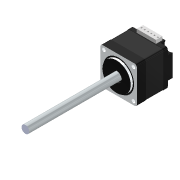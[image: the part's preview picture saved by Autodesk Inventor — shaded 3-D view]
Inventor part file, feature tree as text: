
AUTODESK INVENTOR PART (.ipt)
format: ipt  version: 2022 (Build 260153000, 153)  size: 203,264 bytes
history: mixed  units: mm
features: extrude x1, sketch x1, other x1, imported_body x1
ambient origin geometry x8: Origin, YZ Plane, XZ Plane, XY Plane, X Axis, Y Axis, Z Axis, Center Point
bodies: Volumenkörper1 (imported_parasolid)
feature tree (4):
  extrude  "Extrusion1"  [1 undecoded]
  sketch  "Skizze1"  dims[d0=25.5mm d1=0.0mm]
  other  "Shaft"
  imported_body  NMx_Import_Brep_tag  [imported B-rep: ~112 faces, bbox_mm=[28.5, 31.2, 100.5]]
note: 1 required parameter value undecoded (feature->parameter linkage not recoverable at this tier; creation-order binding heuristic only, values carry confidence <= 0.55)
